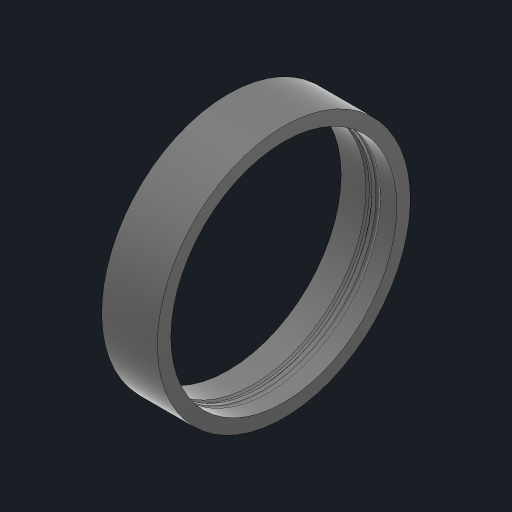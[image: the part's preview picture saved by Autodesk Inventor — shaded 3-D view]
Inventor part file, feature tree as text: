
AUTODESK INVENTOR PART (.ipt)
format: ipt  version: 2023.2 (Build 272271030, 271C)  size: 148,992 bytes
history: native  units: mm
features: revolve x1, sketch x1
ambient origin geometry x8: Origin, YZ Plane, XZ Plane, XY Plane, X Axis, Y Axis, Z Axis, Center Point
bodies: Solid1 (feature_tree)
feature tree (2):
  revolve  "Revolution1"  [1 undecoded]
  sketch  "Sketch1"  dims[d0=2.5mm d1=67.5mm d2=0.5mm d3=75.0mm d4=1.0mm d5=33.0mm d7=4.0mm d8=1.75mm d9=90.0deg d10=67.0mm]
note: 1 required parameter value undecoded (feature->parameter linkage not recoverable at this tier; creation-order binding heuristic only, values carry confidence <= 0.55)
